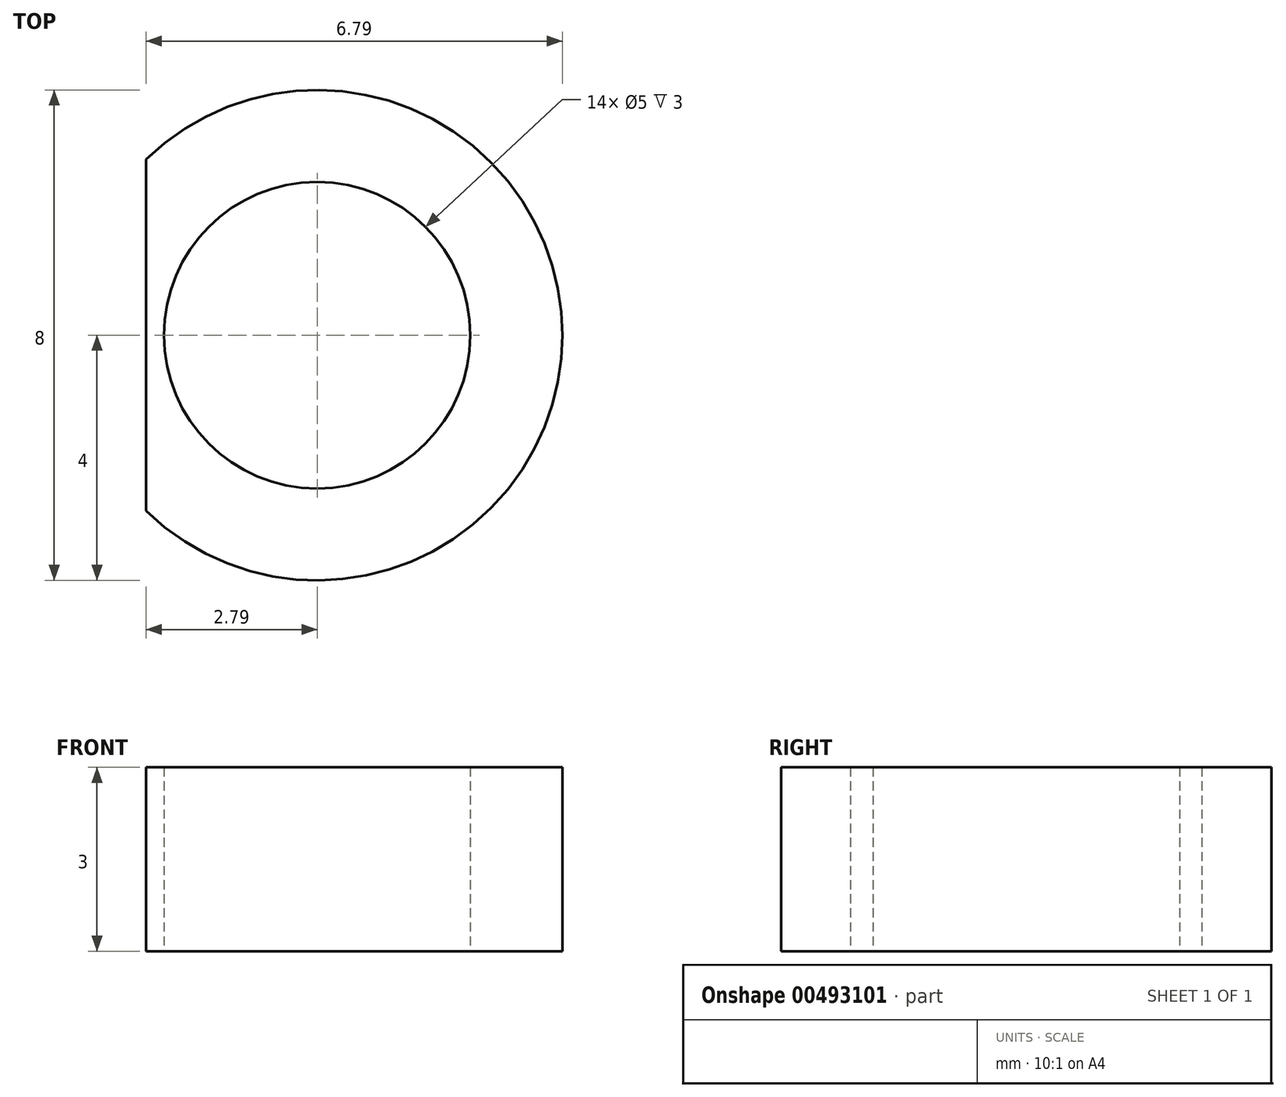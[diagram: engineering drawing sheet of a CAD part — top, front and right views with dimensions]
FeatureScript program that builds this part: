
annotation { "Feature Type Name" : "Feature", "Feature Type Description" : "" }
export const myFeature = defineFeature(function(context is Context, id is Id, definition is map)
    precondition{}
    {
        {
            var Q0;
            Q0=qCreatedBy(makeId("Top.planeOp"),FACE);
            var sketch = newSketch(context, id + "F0", { "sketchPlane" : qUnion([Q0])});
            skArc(sketch, "E0", {"start": v(-2.79, -2.87) * mm, "mid": v(4, 0) * mm, "end": v(-2.79, 2.87) * mm});
            skCircle(sketch, "E1", {"center": v(0, 0) * mm, "radius": 2.5 * mm});
            skLineSegment(sketch, "E2", {"start": v(-2.79, 0) * mm, "end": v(-2.79, 2.87) * mm});
            skLineSegment(sketch, "E3", {"start": v(-2.79, 0) * mm, "end": v(-2.79, -2.87) * mm});
            skSolve(sketch);
        }
        {
            var Q0;
            Q0=makeQuery(id+"F0.imprint","IMPRINT",FACE,{"disambiguationData":[TD([[makeQuery(id+"F0.imprint","IMPRINT",EDGE,{"derivedFrom":sQuery(id+"F0.wireOp",EDGE,"E0")}),1.0]])]});
            extrude(context, id + "F1", {"entities" : qUnion([Q0]), "depth" : 3 * mm});
        }
    });
